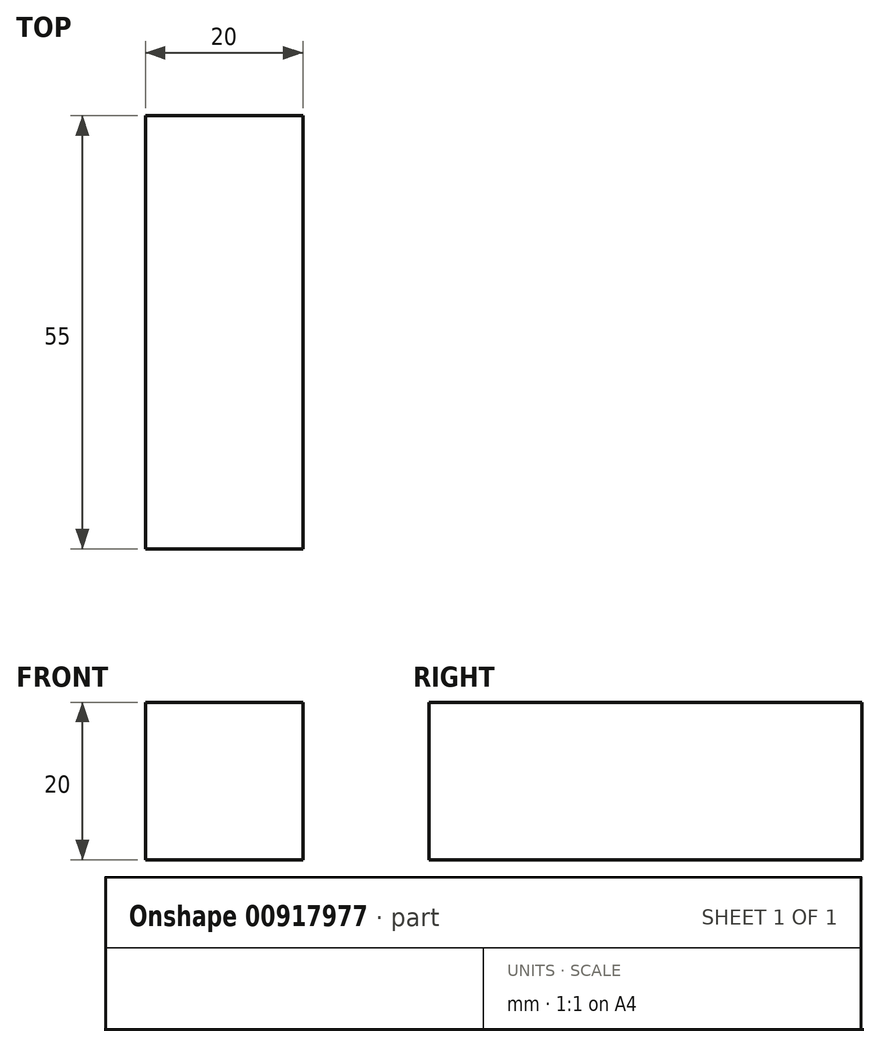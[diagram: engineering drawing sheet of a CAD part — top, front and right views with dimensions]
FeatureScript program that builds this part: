
annotation { "Feature Type Name" : "Feature", "Feature Type Description" : "" }
export const myFeature = defineFeature(function(context is Context, id is Id, definition is map)
    precondition{}
    {
        {
            var Q0;
            Q0=qCreatedBy(makeId("Front.planeOp"),FACE);
            var sketch = newSketch(context, id + "F0", { "sketchPlane" : qUnion([Q0])});
            skLineSegment(sketch, "E0.bottom", {"start": v(0, 0) * mm, "end": v(20, 0) * mm});
            skLineSegment(sketch, "E0.top", {"start": v(0, 20) * mm, "end": v(20, 20) * mm});
            skLineSegment(sketch, "E0.left", {"start": v(0, 0) * mm, "end": v(0, 20) * mm});
            skLineSegment(sketch, "E0.right", {"start": v(20, 0) * mm, "end": v(20, 20) * mm});
            skSolve(sketch);
        }
        {
            var Q0;
            Q0 = qSketchRegion(id + "F0", true);
            extrude(context, id + "F1", {"entities" : qUnion([Q0]), "depth" : 55 * mm, "offsetDistance" : 25 * mm});
        }
    });
